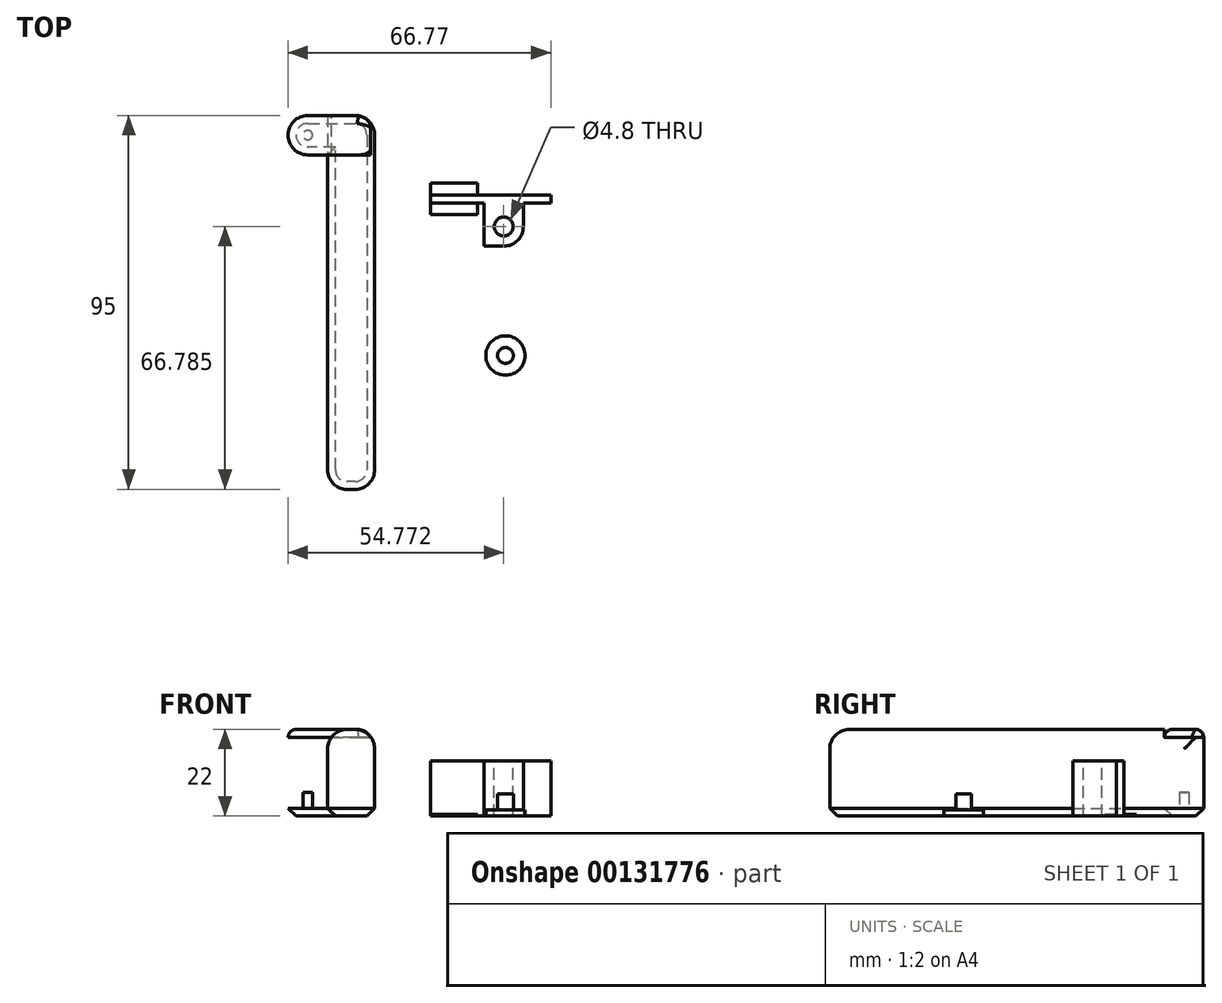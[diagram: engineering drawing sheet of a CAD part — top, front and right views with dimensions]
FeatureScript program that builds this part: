
annotation { "Feature Type Name" : "Feature", "Feature Type Description" : "" }
export const myFeature = defineFeature(function(context is Context, id is Id, definition is map)
    precondition{}
    {
        {
            var Q0;
            Q0=qCreatedBy(makeId("Top.planeOp"),FACE);
            var sketch = newSketch(context, id + "F0", { "sketchPlane" : qUnion([Q0])});
            skLineSegment(sketch, "E0.bottom", {"start": v(-17.84, 42.4) * mm, "end": v(-5.84, 42.4) * mm});
            skLineSegment(sketch, "E0.top", {"start": v(-17.84, -52.6) * mm, "end": v(-5.84, -52.6) * mm});
            skLineSegment(sketch, "E0.left", {"start": v(-17.84, 42.4) * mm, "end": v(-17.84, -52.6) * mm});
            skLineSegment(sketch, "E0.right", {"start": v(-5.84, 42.4) * mm, "end": v(-5.84, -52.6) * mm});
            skSolve(sketch);
        }
        {
            var Q0;
            Q0=makeQuery(id+"F0.imprint","IMPRINT",FACE,{"disambiguationData":[TD([[makeQuery(id+"F0.imprint","IMPRINT",EDGE,{"derivedFrom":sQuery(id+"F0.wireOp",EDGE,"E0.bottom")}),-1.0]])]});
            extrude(context, id + "F1", {"entities" : qUnion([Q0]), "depth" : 22 * mm});
        }
        {
            var Q0;
            Q0=qCreatedBy(makeId("Top.planeOp"),FACE);
            var sketch = newSketch(context, id + "F2", { "sketchPlane" : qUnion([Q0])});
            skLineSegment(sketch, "E1.bottom", {"start": v(-22.84, 42.4) * mm, "end": v(-17.84, 42.4) * mm});
            skLineSegment(sketch, "E1.top", {"start": v(-22.84, 32.4) * mm, "end": v(-17.84, 32.4) * mm});
            skLineSegment(sketch, "E1.right", {"start": v(-17.84, 42.4) * mm, "end": v(-17.84, 32.4) * mm});
            skArc(sketch, "E2", {"start": v(-22.84, 42.4) * mm, "mid": v(-27.84, 37.4) * mm, "end": v(-22.84, 32.4) * mm});
            skSolve(sketch);
        }
        {
            var Q0;
            Q0=makeQuery(id+"F2.imprint","IMPRINT",FACE,{"disambiguationData":[TD([[makeQuery(id+"F2.imprint","IMPRINT",EDGE,{"derivedFrom":sQuery(id+"F2.wireOp",EDGE,"E1.bottom")}),-1.0]])]});
            extrude(context, id + "F3", {"entities" : qUnion([Q0]), "operationType" : NewBodyOperationType.ADD, "depth" : 2 * mm});
        }
        {
            var Q0;
            Q0=makeQuery(id+"F3.opExtrude","CAP_FACE",FACE,{"disambiguationData":[OSD([sQuery(id+"F2.wireOp",EDGE,"E1.bottom"),sQuery(id+"F2.wireOp",EDGE,"E1.top"),sQuery(id+"F2.wireOp",EDGE,"E1.right"),sQuery(id+"F2.wireOp",EDGE,"E2")])],"isStart":false});
            var sketch = newSketch(context, id + "F4", { "sketchPlane" : qUnion([Q0])});
            skCircle(sketch, "E3", {"center": v(-22.84, 37.4) * mm, "radius": 1.2 * mm});
            skSolve(sketch);
        }
        {
            var Q0;
            Q0=makeQuery(id+"F4.imprint","IMPRINT",FACE,{"disambiguationData":[TD([[makeQuery(id+"F4.imprint","IMPRINT",EDGE,{"derivedFrom":sQuery(id+"F4.wireOp",EDGE,"E3")}),1.0]])]});
            extrude(context, id + "F5", {"entities" : qUnion([Q0]), "operationType" : NewBodyOperationType.ADD, "depth" : 4 * mm});
        }
        {
            var Q0;
            Q0=makeQuery(id+"F1.opExtrude","CAP_FACE",FACE,{"disambiguationData":[OSD([sQuery(id+"F0.wireOp",EDGE,"E0.bottom"),sQuery(id+"F0.wireOp",EDGE,"E0.top"),sQuery(id+"F0.wireOp",EDGE,"E0.left"),sQuery(id+"F0.wireOp",EDGE,"E0.right")])],"isStart":false});
            var sketch = newSketch(context, id + "F6", { "sketchPlane" : qUnion([Q0])});
            skLineSegment(sketch, "E4.bottom", {"start": v(-17.84, 42.4) * mm, "end": v(-5.84, 42.4) * mm});
            skLineSegment(sketch, "E4.top", {"start": v(-17.84, 32.4) * mm, "end": v(-5.84, 32.4) * mm});
            skLineSegment(sketch, "E4.left", {"start": v(-17.84, 42.4) * mm, "end": v(-17.84, 32.4) * mm});
            skLineSegment(sketch, "E4.right", {"start": v(-5.84, 42.4) * mm, "end": v(-5.84, 32.4) * mm});
            skSolve(sketch);
        }
        {
            var Q0;
            Q0=makeQuery(id+"F6.imprint","IMPRINT",FACE,{"disambiguationData":[TD([[makeQuery(id+"F6.imprint","IMPRINT",EDGE,{"derivedFrom":sQuery(id+"F6.wireOp",EDGE,"E4.bottom")}),-1.0]])]});
            extrude(context, id + "F7", {"entities" : qUnion([Q0]), "operationType" : NewBodyOperationType.REMOVE, "oppositeDirection" : true, "depth" : 2 * mm});
        }
        {
            var Q0;
            Q0=makeQuery(id+"F1.opExtrude","SWEPT_EDGE",EDGE,{"disambiguationData":[OSD([sQuery(id+"F0.wireOp",EDGE,"E0.bottom"),sQuery(id+"F0.wireOp",EDGE,"E0.right")])]});
            var Q1;
            Q1=makeQuery(id+"F1.opExtrude","SWEPT_EDGE",EDGE,{"disambiguationData":[OSD([sQuery(id+"F0.wireOp",EDGE,"E0.top"),sQuery(id+"F0.wireOp",EDGE,"E0.left")])]});
            var Q2;
            Q2=makeQuery(id+"F1.opExtrude","SWEPT_EDGE",EDGE,{"disambiguationData":[OSD([sQuery(id+"F0.wireOp",EDGE,"E0.top"),sQuery(id+"F0.wireOp",EDGE,"E0.right")])]});
            var Q3;
            Q3=makeQuery(id+"F1.opExtrude","CAP_EDGE",EDGE,{"disambiguationData":[OSD([sQuery(id+"F0.wireOp",EDGE,"E0.right")])],"isStart":false});
            var Q4;
            Q4=makeQuery(id+"F1.opExtrude","CAP_EDGE",EDGE,{"disambiguationData":[OSD([sQuery(id+"F0.wireOp",EDGE,"E0.top")])],"isStart":false});
            var Q5;
            Q5=makeQuery(id+"F1.opExtrude","CAP_EDGE",EDGE,{"disambiguationData":[OSD([sQuery(id+"F0.wireOp",EDGE,"E0.left")])],"isStart":false});
            fillet(context, id + "F8", {"entities" : qUnion([Q0, Q1, Q2, Q3, Q4, Q5]), "radius" : 5 * mm, "tangentPropagation" : true, "allowEdgeOverflow" : false});
        }
        {
            var Q0;
            Q0=makeQuery(id+"F3.boolean.opBoolean","MERGE",FACE,{"derivedFrom":[makeQuery(id+"F1.opExtrude","CAP_FACE",FACE,{"disambiguationData":[OSD([sQuery(id+"F0.wireOp",EDGE,"E0.bottom"),sQuery(id+"F0.wireOp",EDGE,"E0.top"),sQuery(id+"F0.wireOp",EDGE,"E0.left"),sQuery(id+"F0.wireOp",EDGE,"E0.right")])],"isStart":true}),makeQuery(id+"F3.opExtrude","CAP_FACE",FACE,{"disambiguationData":[OSD([sQuery(id+"F2.wireOp",EDGE,"E1.bottom"),sQuery(id+"F2.wireOp",EDGE,"E1.top"),sQuery(id+"F2.wireOp",EDGE,"E1.right"),sQuery(id+"F2.wireOp",EDGE,"E2")])],"isStart":true})]});
            chamfer(context, id + "F9", {"entities" : qUnion([Q0]), "width" : 2 * mm, "tangentPropagation" : true});
        }
        {
            var Q0;
            Q0=makeQuery(id+"F7.boolean.opBoolean","COPY",FACE,{"derivedFrom":makeQuery(id+"F7.opExtrude","CAP_FACE",FACE,{"disambiguationData":[OSD([sQuery(id+"F6.wireOp",EDGE,"E4.bottom"),sQuery(id+"F6.wireOp",EDGE,"E4.top"),sQuery(id+"F6.wireOp",EDGE,"E4.left"),sQuery(id+"F6.wireOp",EDGE,"E4.right")])],"isStart":false})});
            var sketch = newSketch(context, id + "F10", { "sketchPlane" : qUnion([Q0])});
            skLineSegment(sketch, "E5.bottom", {"start": v(-6.84, 42.4) * mm, "end": v(-22.84, 42.4) * mm});
            skLineSegment(sketch, "E5.top", {"start": v(-6.84, 32.4) * mm, "end": v(-22.84, 32.4) * mm});
            skLineSegment(sketch, "E5.left", {"start": v(-6.84, 42.4) * mm, "end": v(-6.84, 32.4) * mm});
            skArc(sketch, "E6", {"start": v(-22.84, 42.4) * mm, "mid": v(-27.84, 37.4) * mm, "end": v(-22.84, 32.4) * mm});
            skSolve(sketch);
        }
        {
            var Q0;
            {var subQ2=sQuery(id+"F10.wireOp",EDGE,"E6");Q0=makeQuery(id+"F10.imprint","IMPRINT",FACE,{"disambiguationData":[TD([[makeQuery(id+"F10.imprint","IMPRINT",EDGE,{"derivedFrom":subQ2}),1.0]])]});}
            var Q1;
            {var subQ1=makeQuery(id+"F7.boolean.opBoolean","COPY",FACE,{"derivedFrom":makeQuery(id+"F7.opExtrude","CAP_FACE",FACE,{"disambiguationData":[OSD([sQuery(id+"F6.wireOp",EDGE,"E4.bottom"),sQuery(id+"F6.wireOp",EDGE,"E4.top"),sQuery(id+"F6.wireOp",EDGE,"E4.left"),sQuery(id+"F6.wireOp",EDGE,"E4.right")])],"isStart":false})});var subQ6=makeQuery(id+"F8.opFillet","BLEND_EDGE",EDGE,{"blendedFrom":[makeQuery(id+"F1.opExtrude","CAP_EDGE",EDGE,{"disambiguationData":[OSD([sQuery(id+"F0.wireOp",EDGE,"E0.left")])],"isStart":false}),subQ1],"blendedInto":[subQ1]});Q1=makeQuery(id+"F10.imprint","IMPRINT",FACE,{"disambiguationData":[TD([[makeQuery(id+"F10.imprint","IMPRINT",EDGE,{"derivedFrom":subQ6}),1.0]])]});}
            extrude(context, id + "F11", {"entities" : qUnion([Q0, Q1]), "depth" : 2 * mm});
        }
        {
            var Q0;
            Q0=makeQuery(id+"F11.opExtrude","CAP_EDGE",EDGE,{"disambiguationData":[OSD([sQuery(id+"F10.wireOp",EDGE,"E5.left")])],"isStart":false});
            fillet(context, id + "F12", {"entities" : qUnion([Q0]), "radius" : 4 * mm, "tangentPropagation" : true, "allowEdgeOverflow" : false});
        }
        {
            var Q0;
            Q0=makeQuery(id+"F11.opExtrude","CAP_EDGE",EDGE,{"disambiguationData":[OSD([sQuery(id+"F10.wireOp",EDGE,"E6")])],"isStart":false});
            var Q1;
            Q1=makeQuery(id+"F11.opExtrude","CAP_EDGE",EDGE,{"disambiguationData":[OSD([sQuery(id+"F10.wireOp",EDGE,"E5.bottom")])],"isStart":false});
            fillet(context, id + "F13", {"entities" : qUnion([Q0, Q1]), "radius" : 2 * mm, "tangentPropagation" : true, "allowEdgeOverflow" : false});
        }
        {
            var Q0;
            Q0=qCreatedBy(makeId("Top.planeOp"),FACE);
            var sketch = newSketch(context, id + "F14", { "sketchPlane" : qUnion([Q0])});
            skLineSegment(sketch, "E7.top", {"start": v(21.93, 9.2) * mm, "end": v(31.93, 9.2) * mm});
            skLineSegment(sketch, "E7.left", {"start": v(21.93, 20.2) * mm, "end": v(21.93, 9.2) * mm});
            skLineSegment(sketch, "E7.right", {"start": v(31.93, 20.2) * mm, "end": v(31.93, 9.2) * mm});
            skLineSegment(sketch, "E8.bottom", {"start": v(21.93, 22.2) * mm, "end": v(38.93, 22.2) * mm});
            skLineSegment(sketch, "E8.top", {"start": v(31.93, 20.2) * mm, "end": v(38.93, 20.2) * mm});
            skLineSegment(sketch, "E8.right", {"start": v(38.93, 22.2) * mm, "end": v(38.93, 20.2) * mm});
            skLineSegment(sketch, "E9.bottom", {"start": v(21.93, 22.2) * mm, "end": v(8.3, 22.2) * mm});
            skLineSegment(sketch, "E9.top", {"start": v(22.3, 20.2) * mm, "end": v(8.3, 20.2) * mm});
            skLineSegment(sketch, "E9.right", {"start": v(8.3, 22.2) * mm, "end": v(8.3, 20.2) * mm});
            skSolve(sketch);
        }
        {
            var Q0;
            Q0 = qSketchRegion(id + "F14", true);
            extrude(context, id + "F15", {"entities" : qUnion([Q0]), "depth" : 14 * mm});
        }
        {
            var Q0;
            Q0=makeQuery(id+"F15.opExtrude","SWEPT_EDGE",EDGE,{"disambiguationData":[OSD([sQuery(id+"F14.wireOp",EDGE,"E7.top"),sQuery(id+"F14.wireOp",EDGE,"E7.right")])]});
            fillet(context, id + "F16", {"entities" : qUnion([Q0]), "radius" : 5 * mm, "tangentPropagation" : true, "allowEdgeOverflow" : false});
        }
        {
            var Q0;
            Q0=makeQuery(id+"F15.opExtrude","CAP_FACE",FACE,{"disambiguationData":[OSD([sQuery(id+"F14.wireOp",EDGE,"E7.top"),sQuery(id+"F14.wireOp",EDGE,"E7.left"),sQuery(id+"F14.wireOp",EDGE,"E7.right"),sQuery(id+"F14.wireOp",EDGE,"E8.bottom"),sQuery(id+"F14.wireOp",EDGE,"E8.top"),sQuery(id+"F14.wireOp",EDGE,"E8.right"),sQuery(id+"F14.wireOp",EDGE,"E9.bottom"),sQuery(id+"F14.wireOp",EDGE,"E9.top"),sQuery(id+"F14.wireOp",EDGE,"E9.right")])],"isStart":false});
            var sketch = newSketch(context, id + "F17", { "sketchPlane" : qUnion([Q0])});
            skCircle(sketch, "E10", {"center": v(26.93, 14.2) * mm, "radius": 2.4 * mm});
            skSolve(sketch);
        }
        {
            var Q0;
            Q0=makeQuery(id+"F17.imprint","IMPRINT",FACE,{"disambiguationData":[TD([[makeQuery(id+"F17.imprint","IMPRINT",EDGE,{"derivedFrom":sQuery(id+"F17.wireOp",EDGE,"E10")}),1.0]])]});
            extrude(context, id + "F18", {"entities" : qUnion([Q0]), "operationType" : NewBodyOperationType.REMOVE, "endBound" : BoundingType.THROUGH_ALL, "oppositeDirection" : true, "depth" : 25 * mm});
        }
        {
            var Q0;
            Q0=qCreatedBy(makeId("Top.planeOp"),FACE);
            var sketch = newSketch(context, id + "F19", { "sketchPlane" : qUnion([Q0])});
            skCircle(sketch, "E11", {"center": v(27.38, -18.57) * mm, "radius": 5 * mm});
            skSolve(sketch);
        }
        {
            var Q0;
            Q0=makeQuery(id+"F19.imprint","IMPRINT",FACE,{"disambiguationData":[TD([[makeQuery(id+"F19.imprint","IMPRINT",EDGE,{"derivedFrom":sQuery(id+"F19.wireOp",EDGE,"E11")}),1.0]])]});
            extrude(context, id + "F20", {"entities" : qUnion([Q0]), "depth" : 1.6 * mm});
        }
        {
            var Q0;
            Q0=makeQuery(id+"F20.opExtrude","CAP_FACE",FACE,{"disambiguationData":[OSD([sQuery(id+"F19.wireOp",EDGE,"E11")])],"isStart":false});
            var sketch = newSketch(context, id + "F21", { "sketchPlane" : qUnion([Q0])});
            skCircle(sketch, "E12", {"center": v(27.38, -18.57) * mm, "radius": 2 * mm});
            skSolve(sketch);
        }
        {
            var Q0;
            Q0=makeQuery(id+"F21.imprint","IMPRINT",FACE,{"disambiguationData":[TD([[makeQuery(id+"F21.imprint","IMPRINT",EDGE,{"derivedFrom":sQuery(id+"F21.wireOp",EDGE,"E12")}),1.0]])]});
            extrude(context, id + "F22", {"entities" : qUnion([Q0]), "operationType" : NewBodyOperationType.ADD, "depth" : 4 * mm});
        }
        {
            var Q0;
            Q0=qCreatedBy(makeId("Top.planeOp"),FACE);
            var sketch = newSketch(context, id + "F23", { "sketchPlane" : qUnion([Q0])});
            skLineSegment(sketch, "E13.bottom", {"start": v(8.3, 25.28) * mm, "end": v(20.3, 25.28) * mm});
            skLineSegment(sketch, "E13.top", {"start": v(8.3, 17.28) * mm, "end": v(20.3, 17.28) * mm});
            skLineSegment(sketch, "E13.left", {"start": v(8.3, 25.28) * mm, "end": v(8.3, 17.28) * mm});
            skLineSegment(sketch, "E13.right", {"start": v(20.3, 25.28) * mm, "end": v(20.3, 17.28) * mm});
            skSolve(sketch);
        }
        {
            var Q0;
            Q0=makeQuery(id+"F23.imprint","IMPRINT",FACE,{"disambiguationData":[TD([[makeQuery(id+"F23.imprint","IMPRINT",EDGE,{"derivedFrom":sQuery(id+"F23.wireOp",EDGE,"E13.bottom")}),-1.0]])]});
            extrude(context, id + "F24", {"entities" : qUnion([Q0]), "operationType" : NewBodyOperationType.ADD, "depth" : .4 * mm});
        }
    });
